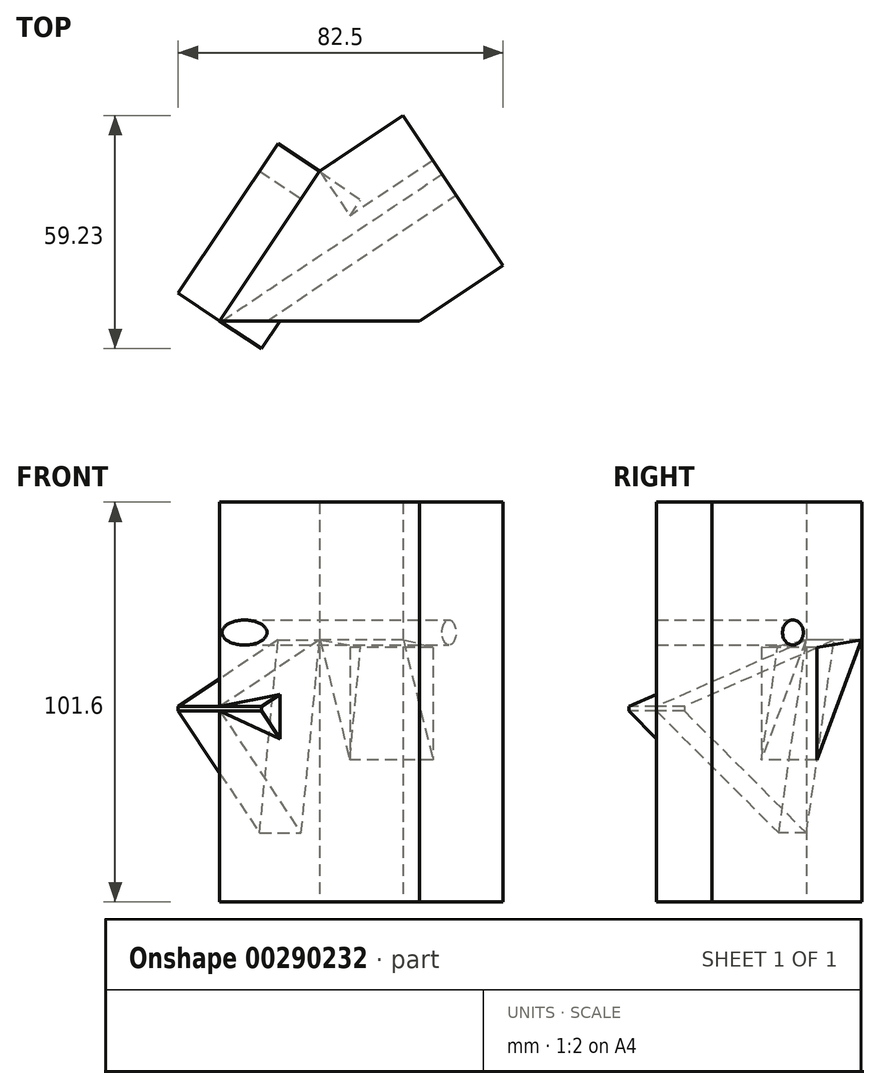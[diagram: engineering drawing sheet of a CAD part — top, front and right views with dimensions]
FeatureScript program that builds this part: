
annotation { "Feature Type Name" : "Feature", "Feature Type Description" : "" }
export const myFeature = defineFeature(function(context is Context, id is Id, definition is map)
    precondition{}
    {
        {
            var Q0;
            Q0=qCreatedBy(makeId("Top.planeOp"),FACE);
            var sketch = newSketch(context, id + "F0", { "sketchPlane" : qUnion([Q0])});
            skLineSegment(sketch, "E0", {"start": v(0, 0) * mm, "end": v(-25.4, -38.1) * mm});
            skLineSegment(sketch, "E1", {"start": v(-25.4, -38.1) * mm, "end": v(25.4, -38.1) * mm});
            skLineSegment(sketch, "E2", {"start": v(25.4, -38.1) * mm, "end": v(0, 0) * mm});
            skSolve(sketch);
        }
        {
            var Q0;
            Q0=makeQuery(id+"F0.imprint","IMPRINT",FACE,{"disambiguationData":[TD([[makeQuery(id+"F0.imprint","IMPRINT",EDGE,{"derivedFrom":sQuery(id+"F0.wireOp",EDGE,"E0")}),1.0]])]});
            extrude(context, id + "F1", {"entities" : qUnion([Q0]), "endBound" : BoundingType.SYMMETRIC, "depth" : 101.6 * mm});
        }
        {
            var Q0;
            Q0=makeQuery(id+"F1.opExtrude","SWEPT_FACE",FACE,{"disambiguationData":[OSD([sQuery(id+"F0.wireOp",EDGE,"E0")])]});
            var sketch = newSketch(context, id + "F2", { "sketchPlane" : qUnion([Q0])});
            skCircle(sketch, "E3.cCircle", {"center": v(18.44, -6.35) * mm, "radius": 14.36 * mm, "construction": true});
            skLineSegment(sketch, "E3.0", {"start": v(0.08, 15.75) * mm, "end": v(46.75, -1.5) * mm});
            skLineSegment(sketch, "E3.1", {"start": v(46.75, -1.5) * mm, "end": v(8.48, -33.3) * mm});
            skLineSegment(sketch, "E3.2", {"start": v(8.48, -33.3) * mm, "end": v(0.08, 15.75) * mm});
            skPoint(sketch, "E3.0.midPoint", {"position": v(23.42, 7.13) * mm});
            skSolve(sketch);
        }
        {
            var Q0;
            {var subQ0=sQuery(id+"F2.wireOp",EDGE,"E3.2");Q0=makeQuery(id+"F2.imprint","IMPRINT",FACE,{"disambiguationData":[TD([[makeQuery(id+"F2.imprint","IMPRINT",EDGE,{"derivedFrom":subQ0}),-1.0]])]});}
            extrude(context, id + "F3", {"entities" : qUnion([Q0]), "operationType" : NewBodyOperationType.ADD, "endBound" : BoundingType.SYMMETRIC, "depth" : 25.4 * mm});
        }
        {
            var Q0;
            Q0=makeQuery(id+"F1.opExtrude","SWEPT_FACE",FACE,{"disambiguationData":[OSD([sQuery(id+"F0.wireOp",EDGE,"E2")])]});
            var sketch = newSketch(context, id + "F4", { "sketchPlane" : qUnion([Q0])});
            skCircle(sketch, "E4", {"center": v(-26.55, -29.26) * mm, "radius": 12.3 * mm});
            skCircle(sketch, "E5", {"center": v(-24.96, -4.76) * mm, "radius": 8.88 * mm});
            skArc(sketch, "E6", {"start": v(-32.02, 26.37) * mm, "mid": v(-22.93, 21.83) * mm, "end": v(-13.53, 25.68) * mm});
            skSolve(sketch);
        }
        {
            var Q0;
            Q0=makeQuery(id+"F4.imprint","IMPRINT",FACE,{"disambiguationData":[TD([[makeQuery(id+"F4.imprint","IMPRINT",EDGE,{"derivedFrom":sQuery(id+"F4.wireOp",EDGE,"E4")}),1.0]])]});
            var Q1;
            Q1=makeQuery(id+"F4.imprint","IMPRINT",FACE,{"disambiguationData":[TD([[makeQuery(id+"F4.imprint","IMPRINT",EDGE,{"derivedFrom":sQuery(id+"F4.wireOp",EDGE,"E5")}),1.0]])]});
            var Q2;
            Q2=makeQuery(id+"F4.imprint","IMPRINT",FACE,{"disambiguationData":[TD([[makeQuery(id+"F4.imprint","IMPRINT",EDGE,{"derivedFrom":sQuery(id+"F4.wireOp",EDGE,"E4")}),-1.0]])]});
            extrude(context, id + "F5", {"entities" : qUnion([Q0, Q1, Q2]), "operationType" : NewBodyOperationType.ADD, "depth" : 25.4 * mm});
        }
        {
            var Q0;
            Q0=makeQuery(id+"F5.opExtrude","CAP_FACE",FACE,{"disambiguationData":[OSD([sQuery(id+"F0.wireOp",EDGE,"E0"),sQuery(id+"F0.wireOp",EDGE,"E1"),sQuery(id+"F0.wireOp",EDGE,"E2"),sQuery(id+"F2.wireOp",EDGE,"E3.0"),sQuery(id+"F2.wireOp",EDGE,"E3.1"),sQuery(id+"F2.wireOp",EDGE,"E3.2")])],"isStart":false});
            var sketch = newSketch(context, id + "F6", { "sketchPlane" : qUnion([Q0])});
            skCircle(sketch, "E7", {"center": v(-21.1, 17.66) * mm, "radius": 8.84 * mm});
            skSolve(sketch);
        }
        {
            var Q0;
            Q0=sQuery(id+"F6.wireOp",VERTEX,"E7.center");
            var Q1;
            Q1=makeQuery(id+"F1.opExtrude","SWEPT_BODY",BODY,{"disambiguationData":[OSD([sQuery(id+"F0.wireOp",EDGE,"E0"),sQuery(id+"F0.wireOp",EDGE,"E1"),sQuery(id+"F0.wireOp",EDGE,"E2")])]});
            hole(context, id + "F7", {"style" : HoleStyle.SIMPLE, "endStyle" : HoleEndStyle.THROUGH, "holeDiameter" : 6.35 * mm, "tappedDepth" : 12.7 * mm, "tapClearance" : 3, "locations" : qUnion([Q0]), "scope" : qUnion([Q1])});
        }
    });
